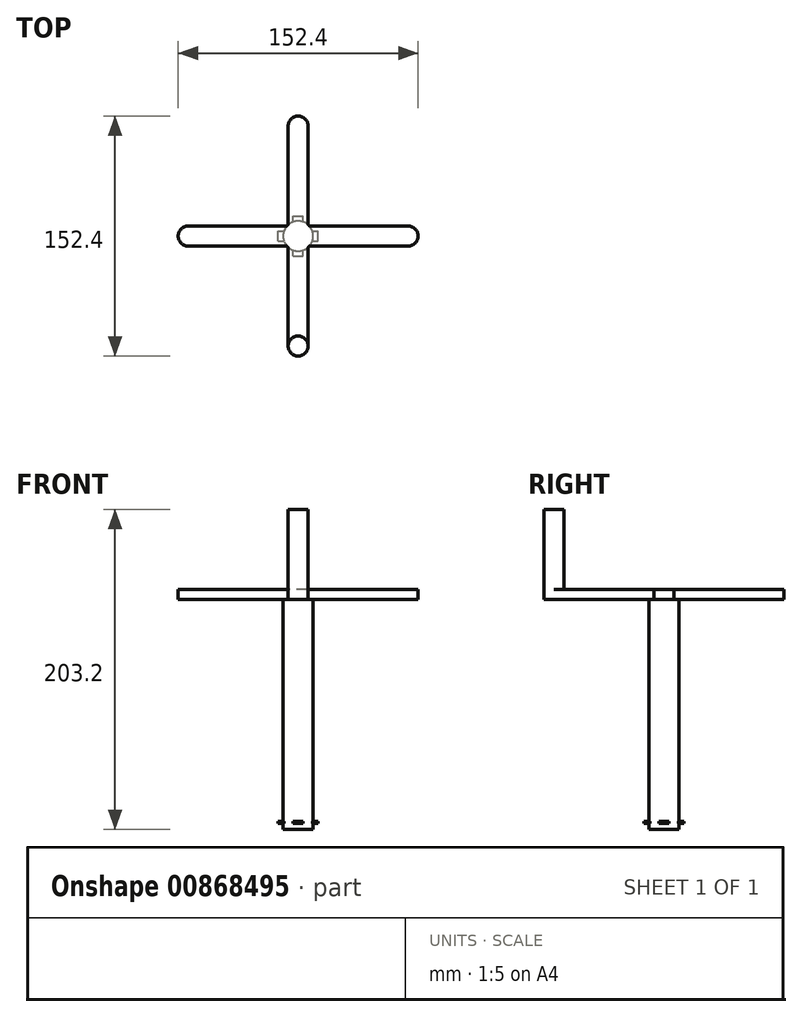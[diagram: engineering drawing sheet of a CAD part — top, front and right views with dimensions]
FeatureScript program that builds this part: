
annotation { "Feature Type Name" : "Feature", "Feature Type Description" : "" }
export const myFeature = defineFeature(function(context is Context, id is Id, definition is map)
    precondition{}
    {
        {
            var Q0;
            Q0=qCreatedBy(makeId("Top.planeOp"),FACE);
            var sketch = newSketch(context, id + "F0", { "sketchPlane" : qUnion([Q0])});
            skCircle(sketch, "E0", {"center": v(0, 0) * mm, "radius": 9.53 * mm});
            skSolve(sketch);
        }
        {
            var Q0;
            Q0 = qSketchRegion(id + "F0", true);
            extrude(context, id + "F1", {"entities" : qUnion([Q0]), "depth" : 152.4 * mm, "offsetDistance" : 25.4 * mm});
        }
        {
            var Q0;
            Q0=makeQuery(id+"F1.opExtrude","CAP_FACE",FACE,{"disambiguationData":[OSD([sQuery(id+"F0.wireOp",EDGE,"E0")])],"isStart":true});
            cPlane(context, id + "F2", {"entities" : qUnion([Q0]), "cplaneType" : CPlaneType.OFFSET, "offset" : 4.44 * mm, "oppositeDirection" : true, "width" : 152.4 * mm, "height" : 152.4 * mm});
        }
        {
            var Q0;
            Q0=qCreatedBy(id+"F2.planeOp",FACE);
            var sketch = newSketch(context, id + "F3", { "sketchPlane" : qUnion([Q0])});
            skLineSegment(sketch, "E1.bottom", {"start": v(-12.7, 3.17) * mm, "end": v(12.7, 3.18) * mm});
            skLineSegment(sketch, "E1.top", {"start": v(-12.7, -3.18) * mm, "end": v(12.7, -3.17) * mm});
            skLineSegment(sketch, "E1.left", {"start": v(-12.7, 3.17) * mm, "end": v(-12.7, -3.18) * mm});
            skLineSegment(sketch, "E1.right", {"start": v(12.7, 3.18) * mm, "end": v(12.7, -3.17) * mm});
            skLineSegment(sketch, "E2.bottom", {"start": v(-3.17, 12.7) * mm, "end": v(3.18, 12.7) * mm});
            skLineSegment(sketch, "E2.top", {"start": v(-3.17, -12.7) * mm, "end": v(3.18, -12.7) * mm});
            skLineSegment(sketch, "E2.left", {"start": v(-3.17, 12.7) * mm, "end": v(-3.17, -12.7) * mm});
            skLineSegment(sketch, "E2.right", {"start": v(3.18, 12.7) * mm, "end": v(3.18, -12.7) * mm});
            skSolve(sketch);
        }
        {
            var Q0;
            Q0 = qSketchRegion(id + "F3", true);
            extrude(context, id + "F4", {"entities" : qUnion([Q0]), "operationType" : NewBodyOperationType.ADD, "endBound" : BoundingType.SYMMETRIC, "depth" : 1.27 * mm, "offsetDistance" : 25.4 * mm});
        }
        {
            var Q0;
            Q0=makeQuery(id+"F1.opExtrude","CAP_FACE",FACE,{"disambiguationData":[OSD([sQuery(id+"F0.wireOp",EDGE,"E0")])],"isStart":false});
            var sketch = newSketch(context, id + "F5", { "sketchPlane" : qUnion([Q0])});
            skLineSegment(sketch, "E3.bottom", {"start": v(-69.85, 6.35) * mm, "end": v(69.85, 6.35) * mm});
            skLineSegment(sketch, "E3.top", {"start": v(-69.85, -6.35) * mm, "end": v(69.85, -6.35) * mm});
            skLineSegment(sketch, "E3.left", {"start": v(-76.2, 0) * mm, "end": v(-76.2, 0) * mm});
            skLineSegment(sketch, "E3.right", {"start": v(76.2, 0) * mm, "end": v(76.2, 0) * mm});
            skLineSegment(sketch, "E4.bottom", {"start": v(0, 76.2) * mm, "end": v(0, 76.2) * mm});
            skLineSegment(sketch, "E4.top", {"start": v(0, -76.2) * mm, "end": v(0, -76.2) * mm});
            skLineSegment(sketch, "E4.left", {"start": v(-6.35, 69.85) * mm, "end": v(-6.35, -69.85) * mm});
            skLineSegment(sketch, "E4.right", {"start": v(6.35, 69.85) * mm, "end": v(6.35, -69.85) * mm});
            skLineSegment(sketch, "E5", {"start": v(0, 71.38) * mm, "end": v(0, -57.03) * mm, "construction": true});
            skLineSegment(sketch, "E6", {"start": v(-32, 0) * mm, "end": v(33.37, 0) * mm, "construction": true});
            skPoint(sketch, "E7.visualSharp", {"position": v(-6.35, -76.2) * mm});
            skArc(sketch, "E7.filletArc", {"start": v(-6.35, -69.85) * mm, "mid": v(-4.5, -74.34) * mm, "end": v(0, -76.2) * mm});
            skPoint(sketch, "E8.visualSharp", {"position": v(6.35, -76.2) * mm});
            skArc(sketch, "E8.filletArc", {"start": v(0, -76.2) * mm, "mid": v(4.5, -74.34) * mm, "end": v(6.35, -69.85) * mm});
            skPoint(sketch, "E9.visualSharp", {"position": v(76.2, -6.35) * mm});
            skArc(sketch, "E9.filletArc", {"start": v(69.85, -6.35) * mm, "mid": v(74.34, -4.5) * mm, "end": v(76.2, 0) * mm});
            skPoint(sketch, "E10.visualSharp", {"position": v(76.2, 6.35) * mm});
            skArc(sketch, "E10.filletArc", {"start": v(76.2, 0) * mm, "mid": v(74.34, 4.5) * mm, "end": v(69.85, 6.35) * mm});
            skPoint(sketch, "E11.visualSharp", {"position": v(6.35, 76.2) * mm});
            skArc(sketch, "E11.filletArc", {"start": v(6.35, 69.85) * mm, "mid": v(4.5, 74.34) * mm, "end": v(0, 76.2) * mm});
            skPoint(sketch, "E12.visualSharp", {"position": v(-6.35, 76.2) * mm});
            skArc(sketch, "E12.filletArc", {"start": v(0, 76.2) * mm, "mid": v(-4.5, 74.34) * mm, "end": v(-6.35, 69.85) * mm});
            skPoint(sketch, "E13.visualSharp", {"position": v(-76.2, 6.35) * mm});
            skArc(sketch, "E13.filletArc", {"start": v(-69.85, 6.35) * mm, "mid": v(-74.34, 4.5) * mm, "end": v(-76.2, 0) * mm});
            skPoint(sketch, "E14.visualSharp", {"position": v(-76.2, -6.35) * mm});
            skArc(sketch, "E14.filletArc", {"start": v(-76.2, 0) * mm, "mid": v(-74.34, -4.5) * mm, "end": v(-69.85, -6.35) * mm});
            skSolve(sketch);
        }
        {
            var Q0;
            Q0 = qSketchRegion(id + "F5", true);
            extrude(context, id + "F6", {"entities" : qUnion([Q0]), "operationType" : NewBodyOperationType.ADD, "oppositeDirection" : true, "depth" : 6.35 * mm, "offsetDistance" : 25.4 * mm});
        }
        {
            var Q0;
            {var subQ0=sQuery(id+"F5.wireOp",EDGE,"E4.right");var subQ1=sQuery(id+"F0.wireOp",EDGE,"E0");Q0=makeQuery(id+"F6.boolean.opBoolean","INTERSECT",EDGE,{"derivedFrom":[makeQuery(id+"F1.opExtrude","SWEPT_FACE",FACE,{"disambiguationData":[OSD([subQ1])]}),makeQuery(id+"F6.opExtrude","SWEPT_FACE",FACE,{"disambiguationData":[OSD([subQ0]),TDD([makeQuery(id+"F5.imprint","IMPRINT",EDGE,{"disambiguationData":[TD([[makeQuery(id+"F5.imprint","INTERSECT",VERTEX,{"derivedFrom":[sQuery(id+"F5.wireOp",EDGE,"E3.top"),subQ0]}),-1.0]])],"derivedFrom":subQ0}),makeQuery(id+"F5.imprint","IMPRINT",EDGE,{"disambiguationData":[TD([[makeQuery(id+"F5.imprint","INTERSECT",VERTEX,{"derivedFrom":[sQuery(id+"F5.wireOp",EDGE,"E4.top"),subQ0]}),1.0]])],"derivedFrom":subQ0})])]})]});}
            var Q1;
            {var subQ0=sQuery(id+"F5.wireOp",EDGE,"E3.top");var subQ1=sQuery(id+"F0.wireOp",EDGE,"E0");Q1=makeQuery(id+"F6.boolean.opBoolean","INTERSECT",EDGE,{"derivedFrom":[makeQuery(id+"F1.opExtrude","SWEPT_FACE",FACE,{"disambiguationData":[OSD([subQ1])]}),makeQuery(id+"F6.opExtrude","SWEPT_FACE",FACE,{"disambiguationData":[OSD([subQ0]),TDD([makeQuery(id+"F5.imprint","IMPRINT",EDGE,{"disambiguationData":[TD([[makeQuery(id+"F5.imprint","INTERSECT",VERTEX,{"derivedFrom":[subQ0,sQuery(id+"F5.wireOp",EDGE,"E4.right")]}),-1.0]])],"derivedFrom":subQ0}),makeQuery(id+"F5.imprint","IMPRINT",EDGE,{"disambiguationData":[TD([[makeQuery(id+"F5.imprint","INTERSECT",VERTEX,{"derivedFrom":[subQ0,sQuery(id+"F5.wireOp",EDGE,"E3.right")]}),1.0]])],"derivedFrom":subQ0})])]})]});}
            var Q2;
            {var subQ0=sQuery(id+"F5.wireOp",EDGE,"E3.bottom");var subQ1=sQuery(id+"F0.wireOp",EDGE,"E0");Q2=makeQuery(id+"F6.boolean.opBoolean","INTERSECT",EDGE,{"derivedFrom":[makeQuery(id+"F1.opExtrude","SWEPT_FACE",FACE,{"disambiguationData":[OSD([subQ1])]}),makeQuery(id+"F6.opExtrude","SWEPT_FACE",FACE,{"disambiguationData":[OSD([subQ0]),TDD([makeQuery(id+"F5.imprint","IMPRINT",EDGE,{"disambiguationData":[TD([[makeQuery(id+"F5.imprint","INTERSECT",VERTEX,{"derivedFrom":[subQ0,sQuery(id+"F5.wireOp",EDGE,"E4.right")]}),-1.0]])],"derivedFrom":subQ0}),makeQuery(id+"F5.imprint","IMPRINT",EDGE,{"disambiguationData":[TD([[makeQuery(id+"F5.imprint","INTERSECT",VERTEX,{"derivedFrom":[subQ0,sQuery(id+"F5.wireOp",EDGE,"E3.right")]}),1.0]])],"derivedFrom":subQ0})])]})]});}
            var Q3;
            {var subQ0=sQuery(id+"F5.wireOp",EDGE,"E4.right");var subQ1=sQuery(id+"F0.wireOp",EDGE,"E0");Q3=makeQuery(id+"F6.boolean.opBoolean","INTERSECT",EDGE,{"derivedFrom":[makeQuery(id+"F1.opExtrude","SWEPT_FACE",FACE,{"disambiguationData":[OSD([subQ1])]}),makeQuery(id+"F6.opExtrude","SWEPT_FACE",FACE,{"disambiguationData":[OSD([subQ0]),TDD([makeQuery(id+"F5.imprint","IMPRINT",EDGE,{"disambiguationData":[TD([[makeQuery(id+"F5.imprint","INTERSECT",VERTEX,{"derivedFrom":[sQuery(id+"F5.wireOp",EDGE,"E4.bottom"),subQ0]}),-1.0]])],"derivedFrom":subQ0}),makeQuery(id+"F5.imprint","IMPRINT",EDGE,{"disambiguationData":[TD([[makeQuery(id+"F5.imprint","INTERSECT",VERTEX,{"derivedFrom":[sQuery(id+"F5.wireOp",EDGE,"E3.bottom"),subQ0]}),1.0]])],"derivedFrom":subQ0})])]})]});}
            var Q4;
            {var subQ0=sQuery(id+"F5.wireOp",EDGE,"E4.left");var subQ1=sQuery(id+"F0.wireOp",EDGE,"E0");Q4=makeQuery(id+"F6.boolean.opBoolean","INTERSECT",EDGE,{"derivedFrom":[makeQuery(id+"F1.opExtrude","SWEPT_FACE",FACE,{"disambiguationData":[OSD([subQ1])]}),makeQuery(id+"F6.opExtrude","SWEPT_FACE",FACE,{"disambiguationData":[OSD([subQ0]),TDD([makeQuery(id+"F5.imprint","IMPRINT",EDGE,{"disambiguationData":[TD([[makeQuery(id+"F5.imprint","INTERSECT",VERTEX,{"derivedFrom":[sQuery(id+"F5.wireOp",EDGE,"E4.bottom"),subQ0]}),-1.0]])],"derivedFrom":subQ0}),makeQuery(id+"F5.imprint","IMPRINT",EDGE,{"disambiguationData":[TD([[makeQuery(id+"F5.imprint","INTERSECT",VERTEX,{"derivedFrom":[sQuery(id+"F5.wireOp",EDGE,"E3.bottom"),subQ0]}),1.0]])],"derivedFrom":subQ0})])]})]});}
            var Q5;
            {var subQ0=sQuery(id+"F5.wireOp",EDGE,"E3.bottom");var subQ1=sQuery(id+"F0.wireOp",EDGE,"E0");Q5=makeQuery(id+"F6.boolean.opBoolean","INTERSECT",EDGE,{"derivedFrom":[makeQuery(id+"F1.opExtrude","SWEPT_FACE",FACE,{"disambiguationData":[OSD([subQ1])]}),makeQuery(id+"F6.opExtrude","SWEPT_FACE",FACE,{"disambiguationData":[OSD([subQ0]),TDD([makeQuery(id+"F5.imprint","IMPRINT",EDGE,{"disambiguationData":[TD([[makeQuery(id+"F5.imprint","INTERSECT",VERTEX,{"derivedFrom":[subQ0,sQuery(id+"F5.wireOp",EDGE,"E3.left")]}),-1.0]])],"derivedFrom":subQ0}),makeQuery(id+"F5.imprint","IMPRINT",EDGE,{"disambiguationData":[TD([[makeQuery(id+"F5.imprint","INTERSECT",VERTEX,{"derivedFrom":[subQ0,sQuery(id+"F5.wireOp",EDGE,"E4.left")]}),1.0]])],"derivedFrom":subQ0})])]})]});}
            var Q6;
            {var subQ0=sQuery(id+"F5.wireOp",EDGE,"E3.top");var subQ1=sQuery(id+"F0.wireOp",EDGE,"E0");Q6=makeQuery(id+"F6.boolean.opBoolean","INTERSECT",EDGE,{"derivedFrom":[makeQuery(id+"F1.opExtrude","SWEPT_FACE",FACE,{"disambiguationData":[OSD([subQ1])]}),makeQuery(id+"F6.opExtrude","SWEPT_FACE",FACE,{"disambiguationData":[OSD([subQ0]),TDD([makeQuery(id+"F5.imprint","IMPRINT",EDGE,{"disambiguationData":[TD([[makeQuery(id+"F5.imprint","INTERSECT",VERTEX,{"derivedFrom":[subQ0,sQuery(id+"F5.wireOp",EDGE,"E3.left")]}),-1.0]])],"derivedFrom":subQ0}),makeQuery(id+"F5.imprint","IMPRINT",EDGE,{"disambiguationData":[TD([[makeQuery(id+"F5.imprint","INTERSECT",VERTEX,{"derivedFrom":[subQ0,sQuery(id+"F5.wireOp",EDGE,"E4.left")]}),1.0]])],"derivedFrom":subQ0})])]})]});}
            var Q7;
            {var subQ0=sQuery(id+"F5.wireOp",EDGE,"E4.left");var subQ1=sQuery(id+"F0.wireOp",EDGE,"E0");Q7=makeQuery(id+"F6.boolean.opBoolean","INTERSECT",EDGE,{"derivedFrom":[makeQuery(id+"F1.opExtrude","SWEPT_FACE",FACE,{"disambiguationData":[OSD([subQ1])]}),makeQuery(id+"F6.opExtrude","SWEPT_FACE",FACE,{"disambiguationData":[OSD([subQ0]),TDD([makeQuery(id+"F5.imprint","IMPRINT",EDGE,{"disambiguationData":[TD([[makeQuery(id+"F5.imprint","INTERSECT",VERTEX,{"derivedFrom":[sQuery(id+"F5.wireOp",EDGE,"E3.top"),subQ0]}),-1.0]])],"derivedFrom":subQ0}),makeQuery(id+"F5.imprint","IMPRINT",EDGE,{"disambiguationData":[TD([[makeQuery(id+"F5.imprint","INTERSECT",VERTEX,{"derivedFrom":[sQuery(id+"F5.wireOp",EDGE,"E4.top"),subQ0]}),1.0]])],"derivedFrom":subQ0})])]})]});}
            fillet(context, id + "F7", {"entities" : qUnion([Q0, Q1, Q2, Q3, Q4, Q5, Q6, Q7]), "radius" : 1.27 * mm, "tangentPropagation" : true, "allowEdgeOverflow" : false});
        }
        {
            var Q0;
            Q0=makeQuery(id+"F6.boolean.opBoolean","MERGE",FACE,{"derivedFrom":[makeQuery(id+"F1.opExtrude","CAP_FACE",FACE,{"disambiguationData":[OSD([sQuery(id+"F0.wireOp",EDGE,"E0")])],"isStart":false}),makeQuery(id+"F6.opExtrude","CAP_FACE",FACE,{"disambiguationData":[OSD([sQuery(id+"F5.wireOp",EDGE,"E3.bottom"),sQuery(id+"F5.wireOp",EDGE,"E3.top"),sQuery(id+"F5.wireOp",EDGE,"E4.left"),sQuery(id+"F5.wireOp",EDGE,"E4.right"),sQuery(id+"F5.wireOp",EDGE,"E7.filletArc"),sQuery(id+"F5.wireOp",EDGE,"E8.filletArc"),sQuery(id+"F5.wireOp",EDGE,"E9.filletArc"),sQuery(id+"F5.wireOp",EDGE,"E10.filletArc"),sQuery(id+"F5.wireOp",EDGE,"E11.filletArc"),sQuery(id+"F5.wireOp",EDGE,"E12.filletArc"),sQuery(id+"F5.wireOp",EDGE,"E13.filletArc"),sQuery(id+"F5.wireOp",EDGE,"E14.filletArc")])],"isStart":true})]});
            var sketch = newSketch(context, id + "F8", { "sketchPlane" : qUnion([Q0])});
            skLineSegment(sketch, "E15", {"start": v(0, -81.74) * mm, "end": v(0, 82.26) * mm});
            skLineSegment(sketch, "E16", {"start": v(90.3, 0) * mm, "end": v(-96.75, 0) * mm});
            skCircle(sketch, "E17", {"center": v(0, -69.85) * mm, "radius": 6.35 * mm});
            skSolve(sketch);
        }
        {
            var Q0;
            Q0 = qSketchRegion(id + "F8", true);
            extrude(context, id + "F9", {"entities" : qUnion([Q0]), "operationType" : NewBodyOperationType.ADD, "depth" : 50.8 * mm, "offsetDistance" : 25.4 * mm});
        }
    });
